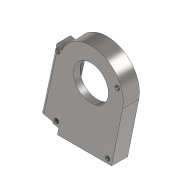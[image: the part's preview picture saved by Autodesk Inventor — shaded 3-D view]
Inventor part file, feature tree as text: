
AUTODESK INVENTOR PART (.ipt)
format: ipt  version: 2020.3 (Build 243373010, 373A)  size: 171,008 bytes
history: native  units: mm
features: sketch x3, extrude x2, projected_geometry x2, delete_face x1, fillet x1
ambient origin geometry x8: Origin, YZ Plane, XZ Plane, XY Plane, X Axis, Y Axis, Z Axis, Center Point
bodies: Body1 (feature_tree)
feature tree (9):
  extrude  "Extrusion4"  Depth=10.0mm
  sketch  "Sketch5"  dims[d26=15.0mm d27=0.0mm d28=92.335mm d29=5.0mm]
  extrude  "Extrusion6"  Depth=5.0mm
  delete_face  "Delete Face1"
  fillet  "Fillet2"  Radius=5.0mm
  sketch  "Sketch4"  dims[d21=10.0mm d22=0.0mm d23=34.0mm]
  projected_geometry  "Projected Loop1"
  sketch  "Sketch6"
  projected_geometry  "Projected Loop2"
